# Revit family: Sink_Floor_Square_Zurn-FS12
name_source: partatom
category: Plumbing Fixtures
units: mm (PartAtom-declared; Revit-internal decimal feet)

## family parameters
Always vertical = Yes
Cut with Voids When Loaded = No
Maintain Annotation Orientation = No
OmniClass Number = 23.70.50.21.24.14
OmniClass Title = Deck Waste Water Drains
Part Type = Normal
Room Calculation Point = No
Round Connector Dimension = Use Radius
Shared = No
Work Plane-Based = No

## types (3) — shared parameters
Assembly Code = D2030300
CW Connection = No
Description = 12 Inch Square Sanitary PVC Floor Sink with 6 3/8 Sump
HW Connection = No
Main Material = PVC- Zurn-White
Manufacturer = Zurn Water, LLC
Manufacurer Brand = Zurn
Model = FS12
Product Documentation Link = https://files.zurn.com
Product Installation Sheet URL = https://files.zurn.com
Product Page URL = https://www.zurn.com
Product data url = https://www.bimobject.com
URL = www.zurn.com
Vent Connection = No
Waste Connection = Yes
zero-valued in all types: Default Elevation

## per-type parameters (varying)
| type | Outlet Outer Radius | Outlet Radius | Type Comments |
| FS12-6-PV2 | 1.546 " | 1 " | FS12-6-PV2 Outlet |
| FS12-6-PV3 | 2.016 " | 1.5 " | FS12-6-PV3 Outlet |
| FS12-6-PV4 | 2.52 " | 2 " | FS12-6-PV4 Outlet |

## geometry (parser evidence)
native form markers: Sweep x4
no freeform markers — native parametric forms only
